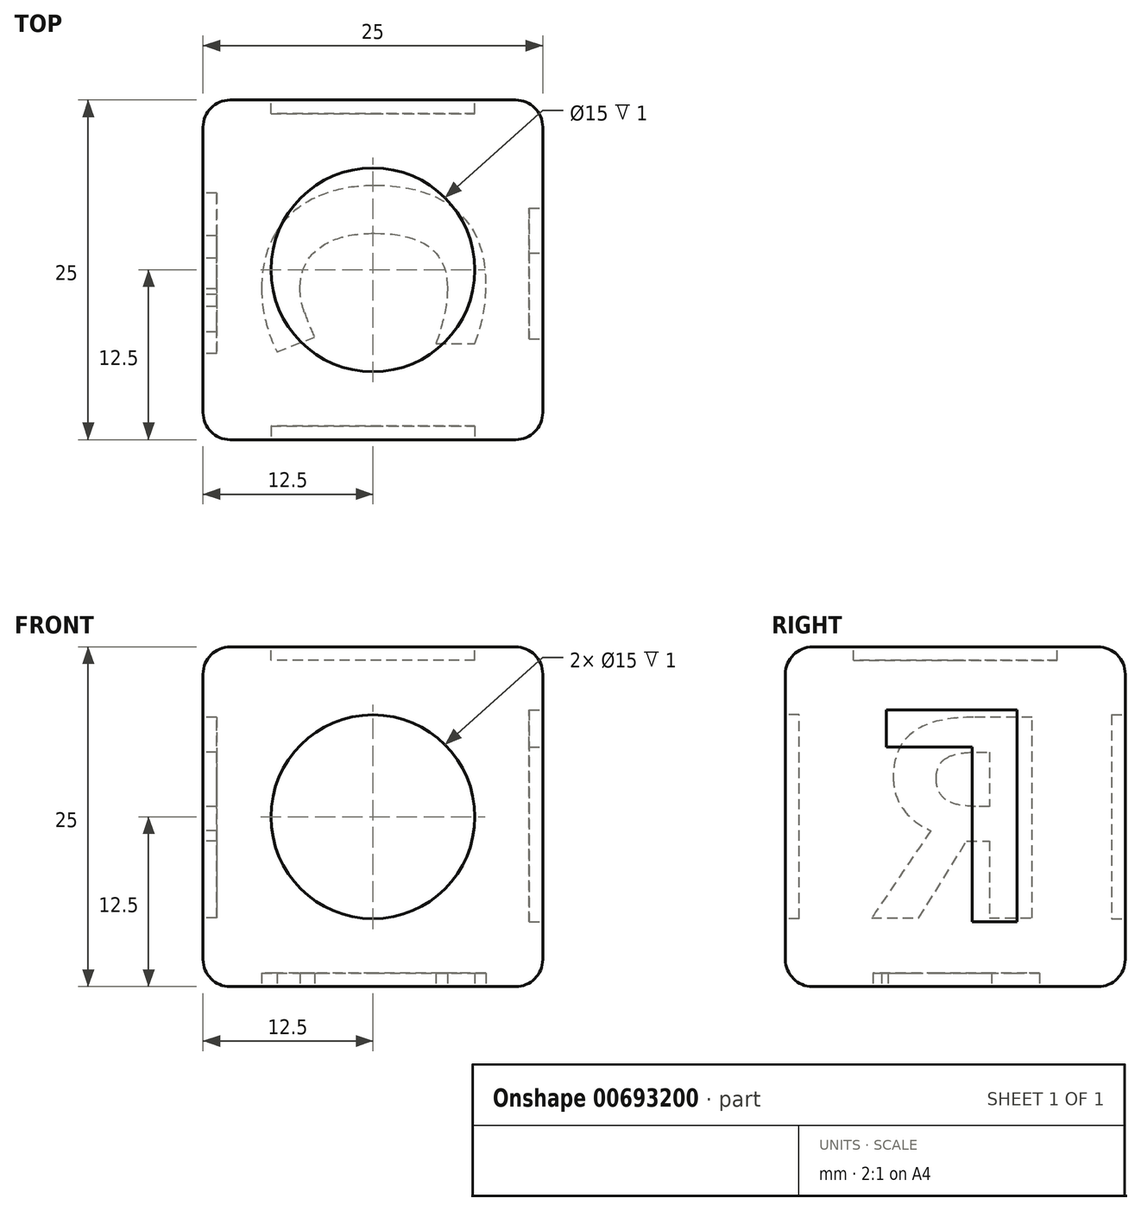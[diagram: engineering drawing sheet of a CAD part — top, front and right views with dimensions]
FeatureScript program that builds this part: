
annotation { "Feature Type Name" : "Feature", "Feature Type Description" : "" }
export const myFeature = defineFeature(function(context is Context, id is Id, definition is map)
    precondition{}
    {
        {
            var Q0;
            Q0=qCreatedBy(makeId("Top.planeOp"),FACE);
            var sketch = newSketch(context, id + "F0", { "sketchPlane" : qUnion([Q0])});
            skLineSegment(sketch, "E0.bottom", {"start": v(12.5, 12.5) * mm, "end": v(-12.5, 12.5) * mm});
            skLineSegment(sketch, "E0.top", {"start": v(12.5, -12.5) * mm, "end": v(-12.5, -12.5) * mm});
            skLineSegment(sketch, "E0.left", {"start": v(12.5, 12.5) * mm, "end": v(12.5, -12.5) * mm});
            skLineSegment(sketch, "E0.right", {"start": v(-12.5, 12.5) * mm, "end": v(-12.5, -12.5) * mm});
            skPoint(sketch, "E0.middle", {"position": v(0, 0) * mm});
            skSolve(sketch);
        }
        {
            var Q0;
            Q0=makeQuery(id+"F0.imprint","IMPRINT",FACE,{"disambiguationData":[TD([[makeQuery(id+"F0.imprint","IMPRINT",EDGE,{"derivedFrom":sQuery(id+"F0.wireOp",EDGE,"E0.bottom")}),1.0]])]});
            extrude(context, id + "F1", {"entities" : qUnion([Q0]), "depth" : 25 * mm, "offsetDistance" : 25 * mm});
        }
        {
            var Q0;
            Q0=makeQuery(id+"F1.opExtrude","CAP_FACE",FACE,{"disambiguationData":[OSD([sQuery(id+"F0.wireOp",EDGE,"E0.bottom"),sQuery(id+"F0.wireOp",EDGE,"E0.top"),sQuery(id+"F0.wireOp",EDGE,"E0.left"),sQuery(id+"F0.wireOp",EDGE,"E0.right")])],"isStart":false});
            var sketch = newSketch(context, id + "F2", { "sketchPlane" : qUnion([Q0])});
            skCircle(sketch, "E1", {"center": v(0, 0) * mm, "radius": 7.5 * mm});
            skSolve(sketch);
        }
        {
            var Q0;
            Q0=makeQuery(id+"F2.imprint","IMPRINT",FACE,{"disambiguationData":[TD([[makeQuery(id+"F2.imprint","IMPRINT",EDGE,{"derivedFrom":sQuery(id+"F2.wireOp",EDGE,"E1")}),1.0]])]});
            extrude(context, id + "F3", {"entities" : qUnion([Q0]), "operationType" : NewBodyOperationType.REMOVE, "oppositeDirection" : true, "depth" : 1 * mm, "offsetDistance" : 25 * mm});
        }
        {
            var Q0;
            Q0=makeQuery(id+"F1.opExtrude","SWEPT_FACE",FACE,{"disambiguationData":[OSD([sQuery(id+"F0.wireOp",EDGE,"E0.top")])]});
            var sketch = newSketch(context, id + "F4", { "sketchPlane" : qUnion([Q0])});
            skCircle(sketch, "E2", {"center": v(0, 12.5) * mm, "radius": 7.5 * mm});
            skPoint(sketch, "E2.centerSnap0", {"position": v(-12.5, 12.5) * mm});
            skSolve(sketch);
        }
        {
            var Q0;
            Q0=makeQuery(id+"F4.imprint","IMPRINT",FACE,{"disambiguationData":[TD([[makeQuery(id+"F4.imprint","IMPRINT",EDGE,{"derivedFrom":sQuery(id+"F4.wireOp",EDGE,"E2")}),1.0]])]});
            extrude(context, id + "F5", {"entities" : qUnion([Q0]), "operationType" : NewBodyOperationType.REMOVE, "oppositeDirection" : true, "depth" : 1 * mm, "offsetDistance" : 25 * mm});
        }
        {
            var Q0;
            Q0=makeQuery(id+"F1.opExtrude","SWEPT_FACE",FACE,{"disambiguationData":[OSD([sQuery(id+"F0.wireOp",EDGE,"E0.bottom")])]});
            var sketch = newSketch(context, id + "F6", { "sketchPlane" : qUnion([Q0])});
            skCircle(sketch, "E3", {"center": v(0, 12.5) * mm, "radius": 7.5 * mm});
            skPoint(sketch, "E3.centerSnap0", {"position": v(12.5, 12.5) * mm});
            skSolve(sketch);
        }
        {
            var Q0;
            Q0=makeQuery(id+"F6.imprint","IMPRINT",FACE,{"disambiguationData":[TD([[makeQuery(id+"F6.imprint","IMPRINT",EDGE,{"derivedFrom":sQuery(id+"F6.wireOp",EDGE,"E3")}),1.0]])]});
            extrude(context, id + "F7", {"entities" : qUnion([Q0]), "operationType" : NewBodyOperationType.REMOVE, "oppositeDirection" : true, "depth" : 1 * mm, "offsetDistance" : 25 * mm});
        }
        {
            var Q0;
            Q0=makeQuery(id+"F1.opExtrude","SWEPT_FACE",FACE,{"disambiguationData":[OSD([sQuery(id+"F0.wireOp",EDGE,"E0.left")])]});
            var sketch = newSketch(context, id + "F8", { "sketchPlane" : qUnion([Q0])});
            skText(sketch, "E4", { "text": "L", "fontName": "OpenSans-Bold.ttf"});
            skLineSegment(sketch, "E5", {"start": v(0, 20.36) * mm, "end": v(0, 25) * mm, "construction": true});
            skLineSegment(sketch, "E6", {"start": v(0, 4.64) * mm, "end": v(0, 0) * mm, "construction": true});
            const initialGuessF8  = {"E4": [0.0065, 0.02036, -1, 0, 0.01571]};
            skSetInitialGuess(sketch, initialGuessF8);
            skSolve(sketch);
        }
        {
            var Q0;
            Q0=makeQuery(id+"F8.imprint","IMPRINT",FACE,{"disambiguationData":[TD([[makeQuery(id+"F8.imprint","IMPRINT",EDGE,{"derivedFrom":sQuery(id+"F8.wireOp",EDGE,"E4.sketch_text.stroke-0")}),-1.0]])]});
            extrude(context, id + "F9", {"entities" : qUnion([Q0]), "operationType" : NewBodyOperationType.REMOVE, "oppositeDirection" : true, "depth" : 1 * mm, "offsetDistance" : 25 * mm});
        }
        {
            var Q0;
            Q0=makeQuery(id+"F1.opExtrude","SWEPT_FACE",FACE,{"disambiguationData":[OSD([sQuery(id+"F0.wireOp",EDGE,"E0.right")])]});
            var sketch = newSketch(context, id + "F10", { "sketchPlane" : qUnion([Q0])});
            skText(sketch, "E7", { "text": "R", "fontName": "OpenSans-Bold.ttf"});
            skLineSegment(sketch, "E8", {"start": v(0, 25) * mm, "end": v(0, 19.95) * mm, "construction": true});
            skLineSegment(sketch, "E9", {"start": v(0, 5.05) * mm, "end": v(0, 0) * mm, "construction": true});
            const initialGuessF10  = {"E7": [-0.0075, 0.00505, 1, 0, 0.0149]};
            skSetInitialGuess(sketch, initialGuessF10);
            skSolve(sketch);
        }
        {
            var Q0;
            Q0=makeQuery(id+"F10.imprint","IMPRINT",FACE,{"disambiguationData":[TD([[makeQuery(id+"F10.imprint","IMPRINT",EDGE,{"derivedFrom":sQuery(id+"F10.wireOp",EDGE,"E7.sketch_text.stroke-0")}),-1.0]])]});
            extrude(context, id + "F11", {"entities" : qUnion([Q0]), "operationType" : NewBodyOperationType.REMOVE, "oppositeDirection" : true, "depth" : 1 * mm, "offsetDistance" : 25 * mm});
        }
        {
            var Q0;
            Q0=makeQuery(id+"F1.opExtrude","CAP_FACE",FACE,{"disambiguationData":[OSD([sQuery(id+"F0.wireOp",EDGE,"E0.bottom"),sQuery(id+"F0.wireOp",EDGE,"E0.top"),sQuery(id+"F0.wireOp",EDGE,"E0.left"),sQuery(id+"F0.wireOp",EDGE,"E0.right")])],"isStart":true});
            var sketch = newSketch(context, id + "F12", { "sketchPlane" : qUnion([Q0])});
            skText(sketch, "E10", { "text": "C", "fontName": "OpenSans-Bold.ttf"});
            skLineSegment(sketch, "E11", {"start": v(-8.1, 0) * mm, "end": v(-12.5, 0) * mm, "construction": true});
            skLineSegment(sketch, "E12", {"start": v(8.1, 0) * mm, "end": v(12.5, 0) * mm, "construction": true});
            const initialGuessF12  = {"E10": [0.0081, -0.0075, 0, 1, 0.0162]};
            skSetInitialGuess(sketch, initialGuessF12);
            skSolve(sketch);
        }
        {
            var Q0;
            Q0=makeQuery(id+"F12.imprint","IMPRINT",FACE,{"disambiguationData":[TD([[makeQuery(id+"F12.imprint","IMPRINT",EDGE,{"derivedFrom":sQuery(id+"F12.wireOp",EDGE,"E10.sketch_text.stroke-0")}),-1.0]])]});
            extrude(context, id + "F13", {"entities" : qUnion([Q0]), "operationType" : NewBodyOperationType.REMOVE, "oppositeDirection" : true, "depth" : 1 * mm, "offsetDistance" : 25 * mm});
        }
        {
            var Q0;
            Q0=makeQuery(id+"F1.opExtrude","CAP_EDGE",EDGE,{"disambiguationData":[OSD([sQuery(id+"F0.wireOp",EDGE,"E0.right")])],"isStart":true});
            var Q1;
            Q1=makeQuery(id+"F1.opExtrude","SWEPT_EDGE",EDGE,{"disambiguationData":[OSD([sQuery(id+"F0.wireOp",EDGE,"E0.bottom"),sQuery(id+"F0.wireOp",EDGE,"E0.right")])]});
            var Q2;
            Q2=makeQuery(id+"F1.opExtrude","CAP_EDGE",EDGE,{"disambiguationData":[OSD([sQuery(id+"F0.wireOp",EDGE,"E0.bottom")])],"isStart":true});
            var Q3;
            Q3=makeQuery(id+"F1.opExtrude","CAP_EDGE",EDGE,{"disambiguationData":[OSD([sQuery(id+"F0.wireOp",EDGE,"E0.bottom")])],"isStart":false});
            var Q4;
            Q4=makeQuery(id+"F1.opExtrude","CAP_EDGE",EDGE,{"disambiguationData":[OSD([sQuery(id+"F0.wireOp",EDGE,"E0.right")])],"isStart":false});
            var Q5;
            Q5=makeQuery(id+"F1.opExtrude","SWEPT_EDGE",EDGE,{"disambiguationData":[OSD([sQuery(id+"F0.wireOp",EDGE,"E0.top"),sQuery(id+"F0.wireOp",EDGE,"E0.right")])]});
            var Q6;
            Q6=makeQuery(id+"F1.opExtrude","CAP_EDGE",EDGE,{"disambiguationData":[OSD([sQuery(id+"F0.wireOp",EDGE,"E0.top")])],"isStart":true});
            var Q7;
            Q7=makeQuery(id+"F1.opExtrude","SWEPT_EDGE",EDGE,{"disambiguationData":[OSD([sQuery(id+"F0.wireOp",EDGE,"E0.top"),sQuery(id+"F0.wireOp",EDGE,"E0.left")])]});
            var Q8;
            Q8=makeQuery(id+"F1.opExtrude","CAP_EDGE",EDGE,{"disambiguationData":[OSD([sQuery(id+"F0.wireOp",EDGE,"E0.left")])],"isStart":true});
            var Q9;
            Q9=makeQuery(id+"F1.opExtrude","CAP_EDGE",EDGE,{"disambiguationData":[OSD([sQuery(id+"F0.wireOp",EDGE,"E0.left")])],"isStart":false});
            var Q10;
            Q10=makeQuery(id+"F1.opExtrude","CAP_EDGE",EDGE,{"disambiguationData":[OSD([sQuery(id+"F0.wireOp",EDGE,"E0.top")])],"isStart":false});
            var Q11;
            Q11=makeQuery(id+"F1.opExtrude","SWEPT_EDGE",EDGE,{"disambiguationData":[OSD([sQuery(id+"F0.wireOp",EDGE,"E0.bottom"),sQuery(id+"F0.wireOp",EDGE,"E0.left")])]});
            fillet(context, id + "F14", {"entities" : qUnion([Q0, Q1, Q2, Q3, Q4, Q5, Q6, Q7, Q8, Q9, Q10, Q11]), "radius" : 2 * mm, "tangentPropagation" : true, "allowEdgeOverflow" : false});
        }
    });
